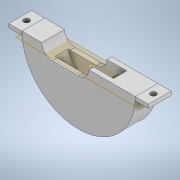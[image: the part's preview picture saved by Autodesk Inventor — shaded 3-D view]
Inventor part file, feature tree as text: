
AUTODESK INVENTOR PART (.ipt)
format: ipt  version: 2022 (Build 260153000, 153)  size: 166,400 bytes
history: native  units: in
note: dims shown in document units (in); Inventor stores cm internally (conversion verified against a paired STEP export)
features: sketch x8, extrude x7, other x2
ambient origin geometry x8: Origin, YZ Plane, XZ Plane, XY Plane, X Axis, Y Axis, Z Axis, Center Point
bodies: Body1 (feature_tree)
feature tree (17):
  other  "Твердое тело1"
  extrude  "Выдавливание1"  Depth=60.0in
  extrude  "Выдавливание2"  Depth=12.0in TaperAngle=0.0deg
  other  "РабПлоскость1"
  extrude  "Выдавливание3"  Depth=32.0in
  extrude  "Выдавливание4"  Depth=7.0in TaperAngle=0.0deg
  extrude  "Выдавливание5"  [1 undecoded]
  extrude  "Выдавливание6"  Depth=5.0in
  sketch  "Эскиз7"
  extrude  "Выдавливание7"  Depth=7.0in TaperAngle=0.0deg
  sketch  "Эскиз1"
  sketch  "Эскиз2"
  sketch  "Эскиз3"
  sketch  "Эскиз4"
  sketch  "Эскиз5"
  sketch  "Эскиз6"
  sketch  "Эскиз8"
note: 1 required parameter value undecoded (feature->parameter linkage not recoverable at this tier; creation-order binding heuristic only, values carry confidence <= 0.55)
